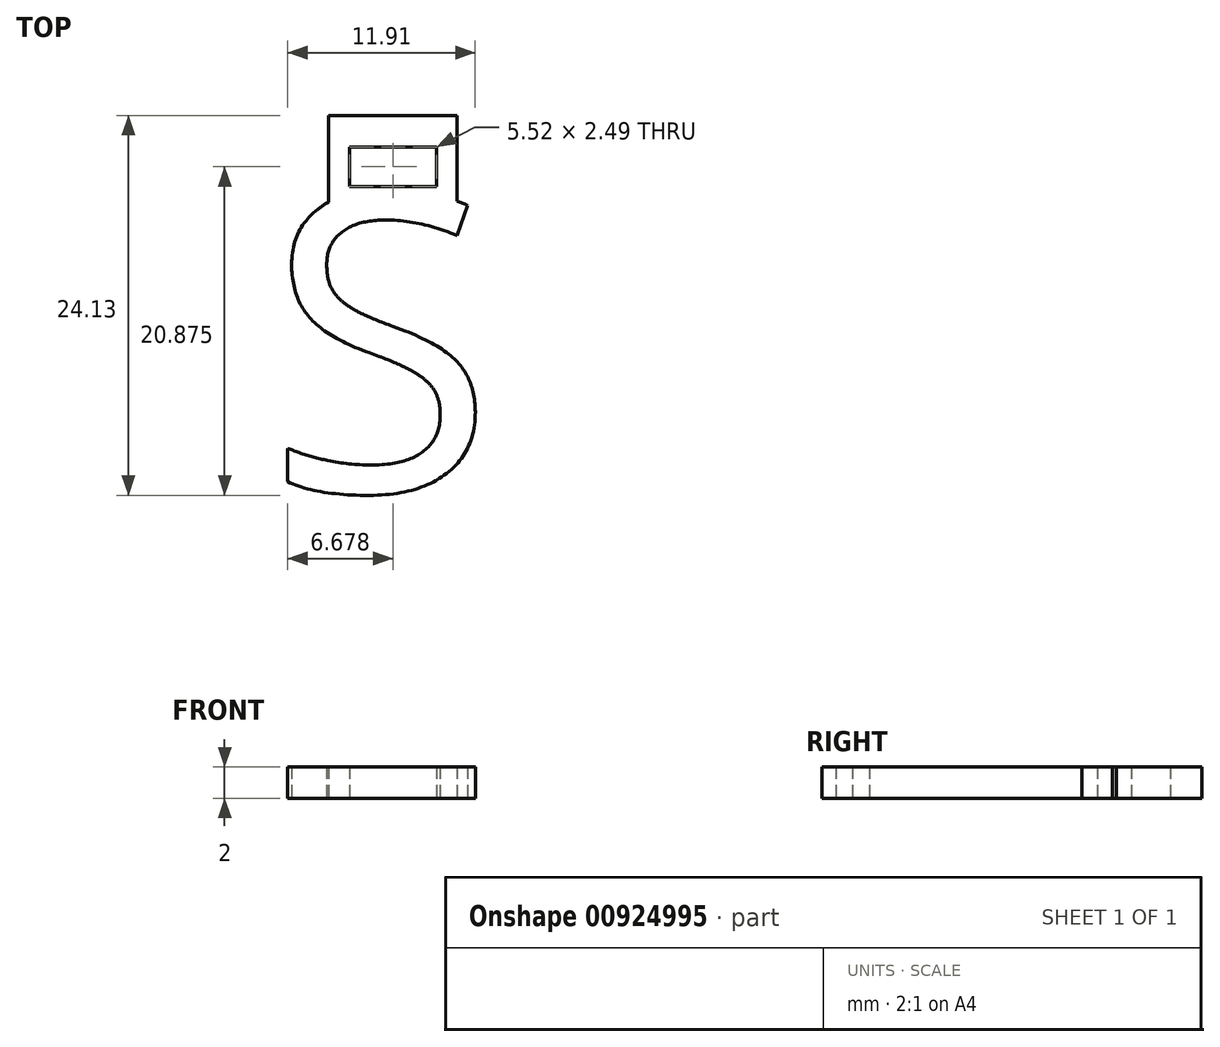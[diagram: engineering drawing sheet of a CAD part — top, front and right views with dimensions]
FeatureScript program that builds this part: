
annotation { "Feature Type Name" : "Feature", "Feature Type Description" : "" }
export const myFeature = defineFeature(function(context is Context, id is Id, definition is map)
    precondition{}
    {
        {
            var Q0;
            Q0=qCreatedBy(makeId("Top.planeOp"),FACE);
            var sketch = newSketch(context, id + "F0", { "sketchPlane" : qUnion([Q0])});
            skText(sketch, "E0", { "text": "S", "fontName": "OpenSans-Regular.ttf"});
            skPoint(sketch, "E1.middle", {"position": v(8.05, 0.72) * mm});
            skLineSegment(sketch, "E2.bottom", {"start": v(12.13, -1.73) * mm, "end": v(3.96, -1.73) * mm});
            skLineSegment(sketch, "E2.left", {"start": v(12.13, -1.73) * mm, "end": v(12.13, 3.18) * mm});
            skLineSegment(sketch, "E2.right", {"start": v(3.96, -1.73) * mm, "end": v(3.96, 3.18) * mm});
            skLineSegment(sketch, "E3", {"start": v(3.96, 3.18) * mm, "end": v(3.96, 4.78) * mm});
            skLineSegment(sketch, "E4", {"start": v(12.13, 3.18) * mm, "end": v(12.13, 4.78) * mm});
            skLineSegment(sketch, "E5", {"start": v(3.96, 4.78) * mm, "end": v(12.13, 4.78) * mm});
            skLineSegment(sketch, "E6", {"start": v(8.05, 4.78) * mm, "end": v(8.05, -1.73) * mm});
            skLineSegment(sketch, "E7.bottom", {"start": v(10.8, 0.28) * mm, "end": v(5.29, 0.28) * mm});
            skLineSegment(sketch, "E7.top", {"start": v(10.8, 2.77) * mm, "end": v(5.29, 2.77) * mm});
            skLineSegment(sketch, "E7.left", {"start": v(10.8, 0.28) * mm, "end": v(10.8, 2.77) * mm});
            skLineSegment(sketch, "E7.right", {"start": v(5.29, 0.28) * mm, "end": v(5.29, 2.77) * mm});
            skPoint(sketch, "E7.middle", {"position": v(8.05, 1.52) * mm});
            const initialGuessF0  = {"E0": [0, -0.01909, 1, 0, 0.01909]};
            skSetInitialGuess(sketch, initialGuessF0);
            skSolve(sketch);
        }
        {
            var Q0;
            Q0 = qSketchRegion(id + "F0", true);
            var Q1;
            {var subQ0=sQuery(id+"F0.wireOp",EDGE,"E8C4UfHz-qXCL-YPa0-fCWr-jR2j1qNFgARm.bottom");Q1=makeQuery(id+"F0.imprint","IMPRINT",FACE,{"disambiguationData":[TD([[makeQuery(id+"F0.imprint","IMPRINT",EDGE,{"derivedFrom":subQ0}),-1.0]])]});}
            extrude(context, id + "F1", {"entities" : qUnion([Q0, Q1]), "depth" : 2 * mm, "offsetDistance" : 25 * mm});
        }
    });
